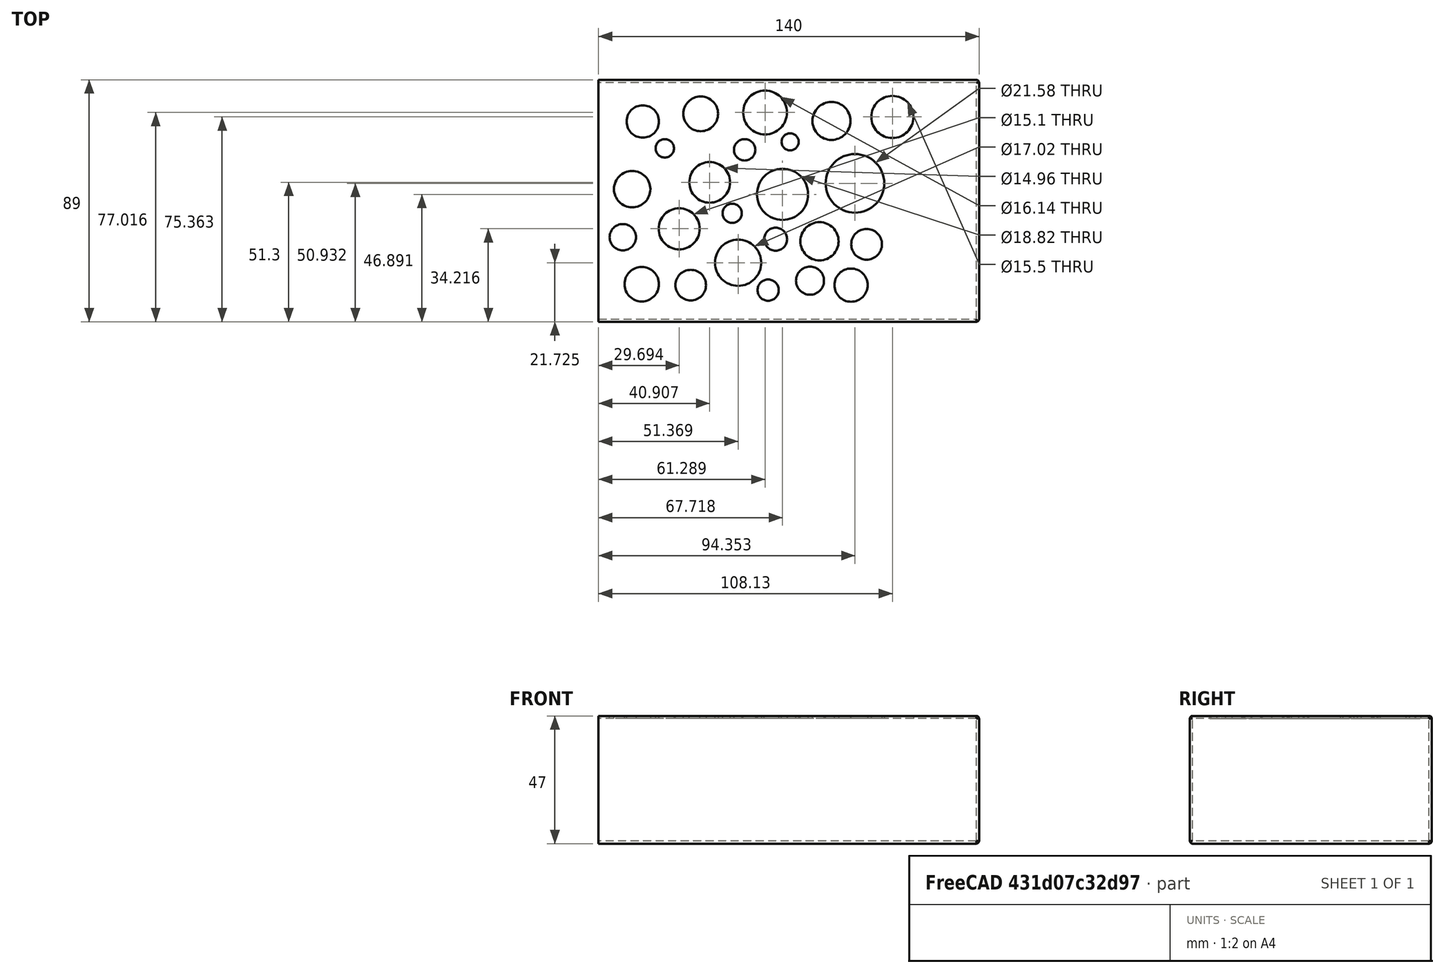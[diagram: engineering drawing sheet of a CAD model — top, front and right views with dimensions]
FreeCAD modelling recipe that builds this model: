
FCSTD DOCUMENT  (FreeCAD 0.18R4 (GitTag))
Label: v2 filter holder
License: All rights reserved
LicenseURL: http://en.wikipedia.org/wiki/All_rights_reserved
objects: Sketcher::SketchObject×2, PartDesign::Pad×1, PartDesign::Thickness×1, PartDesign::Pocket×1, PartDesign::Body×1
note: 8 computed .brp shape members not serialized (recipe doc carries the construction recipe); baked Part::Feature solids carry a one-line shape summary decoded from their .brp

FEATURE [Sketcher::SketchObject] Sketch001
  MapMode = 5
  sketch-geometry (4):
    g0: LineSegment StartX=-98.6361 StartY=-57.4943 StartZ=0 EndX=40.3639 EndY=-57.4943 EndZ=0
    g1: LineSegment StartX=40.3639 StartY=-57.4943 StartZ=0 EndX=40.3639 EndY=29.5057 EndZ=0
    g2: LineSegment StartX=40.3639 StartY=29.5057 StartZ=0 EndX=-98.6361 EndY=29.5057 EndZ=0
    g3: LineSegment StartX=-98.6361 StartY=29.5057 StartZ=0 EndX=-98.6361 EndY=-57.4943 EndZ=0
  constraints (10):
    c: Coincident(g0,g1)
    c: Coincident(g1,g2)
    c: Coincident(g2,g3)
    c: Coincident(g3,g0)
    c: Horizontal(g0)
    c: Horizontal(g2)
    c: Vertical(g1)
    c: Vertical(g3)
    c: DistanceY(g0,g1) = 87
    c: DistanceX(g2,g1) = 139
FEATURE [PartDesign::Pad] Pad
  Length = 45
  Length2 = 100
  Profile = -> Sketch001
  Type = 0
FEATURE [PartDesign::Thickness] Thickness
  Base = -> Pad [Face4]
  BaseFeature = -> Pad
  Join = 0
  Mode = 0
  Value = 1
FEATURE [Sketcher::SketchObject] Sketch002
  MapMode = 5
  Placement = pos=(0,0,46) rot=(0,0,1;0rad)
  Support = -> [Thickness]
  sketch-geometry (23):
    g0: Circle CenterX=-82.3346 CenterY=15.2163 CenterZ=0 NormalX=0 NormalY=0 NormalZ=1 AngleXU=0 Radius=5.94705
    g1: Circle CenterX=-61.0213 CenterY=18.0212 CenterZ=0 NormalX=0 NormalY=0 NormalZ=1 AngleXU=0 Radius=6.39154
    g2: Circle CenterX=-57.7329 CenterY=-7.18999 CenterZ=0 NormalX=0 NormalY=0 NormalZ=1 AngleXU=0 Radius=7.47971
    g3: Circle CenterX=-86.2325 CenterY=-9.65631 CenterZ=0 NormalX=0 NormalY=0 NormalZ=1 AngleXU=0 Radius=6.69004
    g4: Circle CenterX=-68.9463 CenterY=-24.274 CenterZ=0 NormalX=0 NormalY=0 NormalZ=1 AngleXU=0 Radius=7.55147
    g5: Circle CenterX=-82.7231 CenterY=-44.6637 CenterZ=0 NormalX=0 NormalY=0 NormalZ=1 AngleXU=0 Radius=6.34199
    g6: Circle CenterX=-47.2707 CenterY=-36.765 CenterZ=0 NormalX=0 NormalY=0 NormalZ=1 AngleXU=0 Radius=8.50949
    g7: Circle CenterX=-30.9222 CenterY=-11.5993 CenterZ=0 NormalX=0 NormalY=0 NormalZ=1 AngleXU=0 Radius=9.40958
    g8: Circle CenterX=-37.3514 CenterY=18.526 CenterZ=0 NormalX=0 NormalY=0 NormalZ=1 AngleXU=0 Radius=8.06988
    g9: Circle CenterX=-17.3291 CenterY=-28.8663 CenterZ=0 NormalX=0 NormalY=0 NormalZ=1 AngleXU=0 Radius=7.03083
    g10: Circle CenterX=-20.8192 CenterY=-43.3779 CenterZ=0 NormalX=0 NormalY=0 NormalZ=1 AngleXU=0 Radius=5.14662
    g11: Circle CenterX=-12.9205 CenterY=15.4033 CenterZ=0 NormalX=0 NormalY=0 NormalZ=1 AngleXU=0 Radius=6.98267
    g12: Circle CenterX=-4.28699 CenterY=-7.55813 CenterZ=0 NormalX=0 NormalY=0 NormalZ=1 AngleXU=0 Radius=10.7878
    g13: Circle CenterX=0 CenterY=-29.9684 CenterZ=0 NormalX=0 NormalY=0 NormalZ=1 AngleXU=0 Radius=5.65876
    g14: Circle CenterX=-44.8587 CenterY=4.77725 CenterZ=0 NormalX=0 NormalY=0 NormalZ=1 AngleXU=0 Radius=3.93116
    g15: Circle CenterX=-74.2492 CenterY=5.32832 CenterZ=0 NormalX=0 NormalY=0 NormalZ=1 AngleXU=0 Radius=3.37712
    g16: Circle CenterX=-64.6973 CenterY=-45.003 CenterZ=0 NormalX=0 NormalY=0 NormalZ=1 AngleXU=0 Radius=5.62287
    g17: Circle CenterX=-36.2252 CenterY=-46.84 CenterZ=0 NormalX=0 NormalY=0 NormalZ=1 AngleXU=0 Radius=3.90532
    g18: Circle CenterX=-33.4698 CenterY=-28.1035 CenterZ=0 NormalX=0 NormalY=0 NormalZ=1 AngleXU=0 Radius=4.22889
    g19: Circle CenterX=-49.4509 CenterY=-18.5515 CenterZ=0 NormalX=0 NormalY=0 NormalZ=1 AngleXU=0 Radius=3.52859
    g20: Circle CenterX=-28.1428 CenterY=7.71631 CenterZ=0 NormalX=0 NormalY=0 NormalZ=1 AngleXU=0 Radius=3.16034
    g21: Circle CenterX=-5.73246 CenterY=-45.003 CenterZ=0 NormalX=0 NormalY=0 NormalZ=1 AngleXU=0 Radius=6.10618
    g22: Circle CenterX=-89.6793 CenterY=-27.3687 CenterZ=0 NormalX=0 NormalY=0 NormalZ=1 AngleXU=0 Radius=4.85306
  constraints (1):
    c: PointOnObject(g13,g-2)
FEATURE [PartDesign::Pocket] Pocket
  BaseFeature = -> Thickness
  Length = 5
  Length2 = 100
  Profile = -> Sketch002
  Type = 0
FEATURE [PartDesign::Body] Body001
  Group = -> [Sketch001,Pad,Thickness,Sketch002,Pocket]
  Origin = -> Origin001
  Tip = -> Pocket
